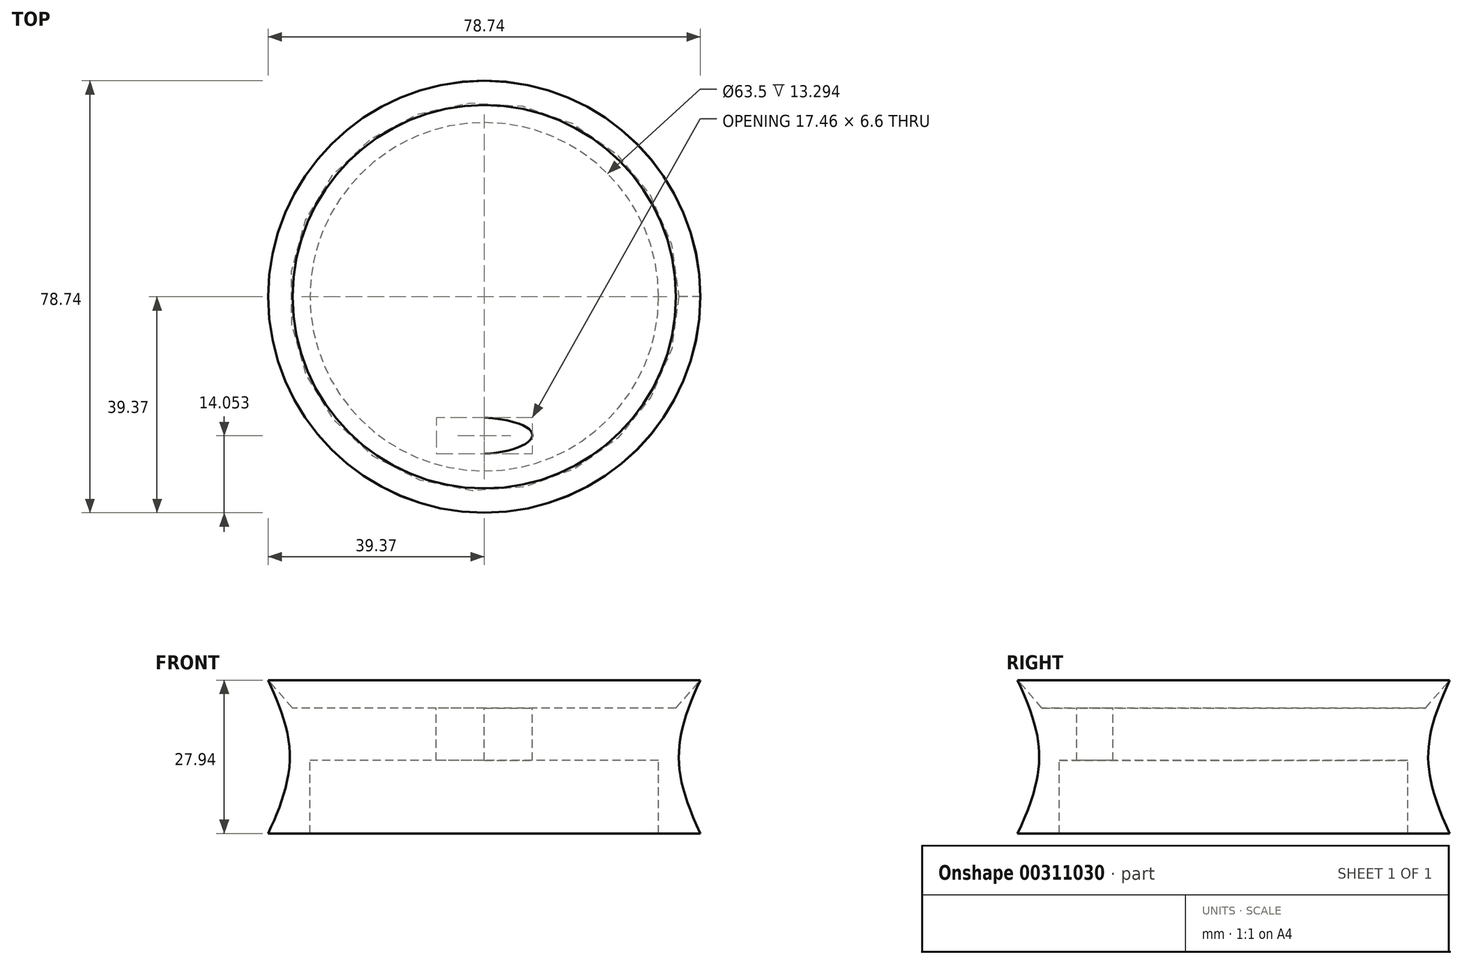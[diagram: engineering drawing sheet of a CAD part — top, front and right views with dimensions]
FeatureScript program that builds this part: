
annotation { "Feature Type Name" : "Feature", "Feature Type Description" : "" }
export const myFeature = defineFeature(function(context is Context, id is Id, definition is map)
    precondition{}
    {
        {
            var Q0;
            Q0=qCreatedBy(makeId("Front.planeOp"),FACE);
            var sketch = newSketch(context, id + "F0", { "sketchPlane" : qUnion([Q0])});
            skLineSegment(sketch, "E0", {"start": v(0, 39.35) * mm, "end": v(39.37, 39.35) * mm});
            skLineSegment(sketch, "E1", {"start": v(0, 11.4) * mm, "end": v(39.37, 11.4) * mm});
            skFitSpline(sketch, "E2", {"points": [v(39.37, 39.35) * mm, v(39.37, 11.4) * mm], "startDerivative": vector(-14.77, -32.22) * mm, "endDerivative": vector(16.66, -35.52) * mm});
            skLineSegment(sketch, "E3", {"start": v(0, 24.7) * mm, "end": v(31.75, 24.7) * mm});
            skLineSegment(sketch, "E4", {"start": v(31.75, 24.7) * mm, "end": v(31.75, 11.4) * mm});
            skLineSegment(sketch, "E5", {"start": v(39.36, 39.35) * mm, "end": v(34.94, 34.27) * mm});
            skLineSegment(sketch, "E6", {"start": v(34.94, 34.27) * mm, "end": v(0, 34.27) * mm});
            skLineSegment(sketch, "E7", {"start": v(0, 59.6) * mm, "end": v(0, -34.6) * mm, "construction": true});
            skLineSegment(sketch, "E8", {"start": v(0, 39.35) * mm, "end": v(0, 11.4) * mm});
            skSolve(sketch);
        }
        {
            var Q0;
            {var subQ1=sQuery(id+"F0.wireOp",EDGE,"E2");Q0=makeQuery(id+"F0.imprint","IMPRINT",FACE,{"disambiguationData":[TD([[makeQuery(id+"F0.imprint","IMPRINT",EDGE,{"derivedFrom":subQ1}),-1.0]])]});}
            var Q1;
            Q1=sQuery(id+"F0.wireOp",EDGE,"E7");
            revolve(context, id + "F1", {"entities" : qUnion([Q0]), "axis" : qUnion([Q1]), "revolveType" : RevolveType.FULL});
        }
        {
            var Q0;
            Q0=qCreatedBy(makeId("Top.planeOp"),FACE);
            var sketch = newSketch(context, id + "F2", { "sketchPlane" : qUnion([Q0])});
            skFitSpline(sketch, "E9", {"points": [v(0, -22.02) * mm, v(-8.73, -25.5) * mm, v(0, -28.62) * mm], "startDerivative": vector(-36.84, -2.54) * mm, "endDerivative": vector(26.45, -0.88) * mm});
            skLineSegment(sketch, "E10", {"start": v(0, 63.9) * mm, "end": v(0, -60.68) * mm, "construction": true});
            skFitSpline(sketch, "E11.MirrorCS", {"points": [v(0, -22.02) * mm, v(8.73, -25.5) * mm, v(0, -28.62) * mm], "startDerivative": vector(36.84, -2.54) * mm, "endDerivative": vector(-26.45, -0.88) * mm});
            skSolve(sketch);
        }
        {
            var Q0;
            Q0=makeQuery(id+"F2.imprint","IMPRINT",FACE,{"disambiguationData":[TD([[makeQuery(id+"F2.imprint","IMPRINT",EDGE,{"derivedFrom":sQuery(id+"F2.wireOp",EDGE,"E9")}),1.0]])]});
            extrude(context, id + "F3", {"entities" : qUnion([Q0]), "operationType" : NewBodyOperationType.REMOVE, "endBound" : BoundingType.SYMMETRIC, "oppositeDirection" : true, "depth" : 127 * mm});
        }
    });
